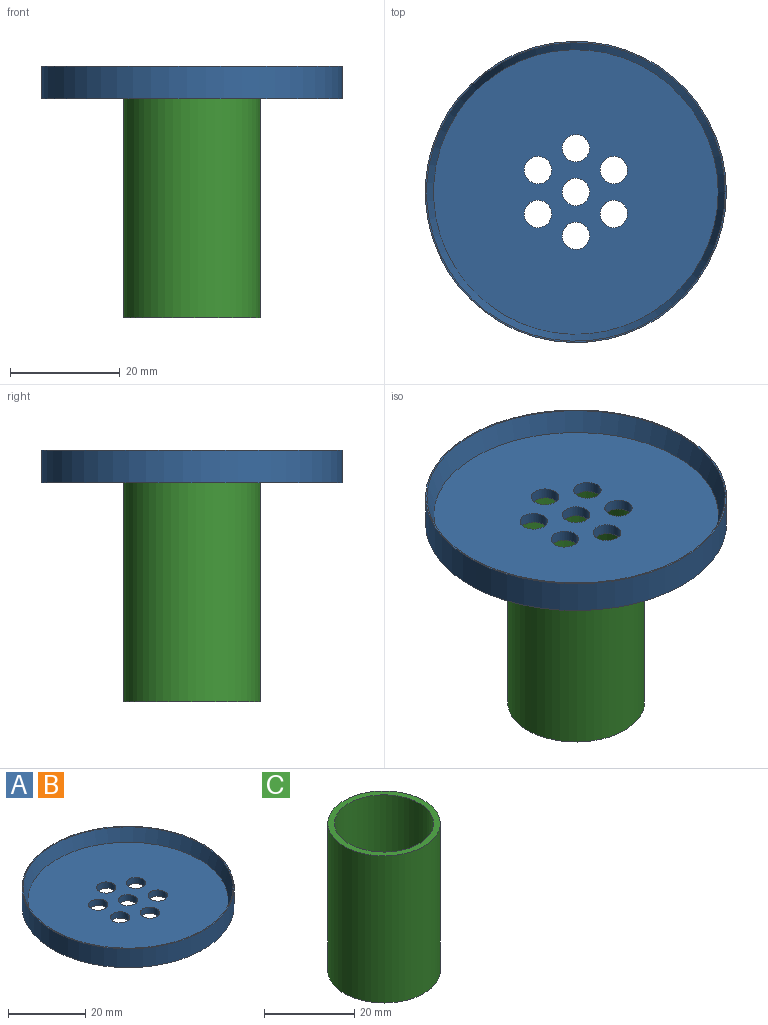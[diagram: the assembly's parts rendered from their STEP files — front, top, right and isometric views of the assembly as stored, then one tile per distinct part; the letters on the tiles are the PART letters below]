
ASSEMBLY  parts=3 mates=1
PART A: 12 faces, bbox 55x55x6 mm
  f0: cylinder r=2.5mm len=5mm, axis (0,0,-1), area 31.4mm2, adj f7,f8
  f1: cylinder r=2.5mm len=5mm, axis (0,0,-1), area 31.4mm2, adj f7,f8
  f2: cylinder r=2.5mm len=5mm, axis (0,0,-1), area 31.4mm2, adj f7,f8
  f3: cylinder r=2.5mm len=5mm, axis (0,0,-1), area 31.4mm2, adj f7,f8
  f4: cylinder r=2.5mm len=5mm, axis (0,0,-1), area 31.4mm2, adj f7,f8
  f5: cylinder r=2.5mm len=5mm, axis (0,0,-1), area 31.4mm2, adj f7,f8
  f6: cylinder r=2.5mm len=5mm, axis (0,0,-1), area 31.4mm2, adj f7,f8
  f7: plane 52x52mm, normal (0,0,1), area 1986.3mm2, adj f0,f1,f2,f3,f4,f5,f6,f11
  f8: plane 55x55mm, normal (0,0,-1), area 2238.4mm2, adj f0,f1,f2,f3,f4,f5,f6,f9
  f9: cylinder r=27.5mm len=55mm, axis (0,0,-1), area 1036.7mm2, adj f8,f10
  f10: plane 55x55mm, normal (0,0,1), area 43mm2, adj f9,f11
  f11: cone r=26mm half-angle=17.4deg, axis (0,0,1), area 701.1mm2, adj f7,f10
PART B: same geometry as A
PART C: 4 faces, bbox 25x25x40 mm
  f0: cylinder r=11mm len=40mm, axis (0,0,-1), area 2764.6mm2, adj f2,f3
  f1: cylinder r=12.5mm len=40mm, axis (0,0,-1), area 3141.6mm2, adj f2,f3
  f2: plane 25x25mm, normal (0,0,1), area 110.7mm2, adj f0,f1
  f3: plane 25x25mm, normal (0,0,-1), area 110.7mm2, adj f0,f1
PLACE A t=(-2.72,3.28,-5.22)mm
PLACE B t=(-2.72,3.28,-5.22)mm
PLACE C t=(-2.72,3.28,-45.22)mm
MATE fastened C.f0 <-> A.f9  axis (0,0,-1) through (-2.72,3.28,-5.22)mm
